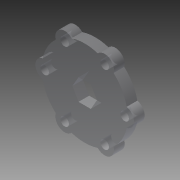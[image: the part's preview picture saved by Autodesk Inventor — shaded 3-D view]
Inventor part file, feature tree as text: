
AUTODESK INVENTOR PART (.ipt)
format: ipt  version: 2013 (Build 170138000, 138)  size: 141,312 bytes
history: native  units: in
note: dims shown in document units (in); Inventor stores cm internally (conversion verified against a paired STEP export)
features: extrude x1, sketch x1, reference x1
ambient origin geometry x8: Origin, YZ Plane, XZ Plane, XY Plane, X Axis, Y Axis, Z Axis, Center Point
bodies: Solid1 (feature_tree)
feature tree (3):
  extrude  "Extrusion1"  Depth=0.25in TaperAngle=0.0deg
  sketch  "Sketch1"  dims[d0=0.5in d1=0.25in d2=0.0in]
  reference  "Reference2"
